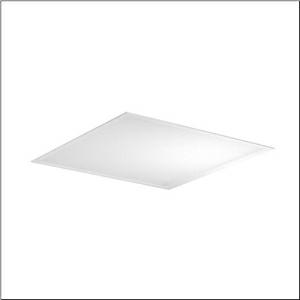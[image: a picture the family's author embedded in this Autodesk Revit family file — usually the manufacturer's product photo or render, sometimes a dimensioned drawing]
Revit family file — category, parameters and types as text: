
# Revit family: apollon_31_square_51mp12wd2m42
name_source: partatom
category: Lighting Fixtures
units: mm (PartAtom-declared; Revit-internal decimal feet)

## family parameters
Cut with Voids When Loaded = No
Host = Face
Light Source = No
Part Type = Normal
Room Calculation Point = No
Round Connector Dimension = Use Diameter
Shared = No

## types (1)
- --- (1 x LED, 4000 lm, 27.5 W, 4000K)
    Apparent Load = 28 VA
    CIE Flux Codes = 62 87 97 100 100
    Color Rendering = 80
    Color Temperature = 4000K
    Default Elevation = 1800 mm
    Description = Apollon 31 square, office luminaire, primary optical cover: micro prismatic cover, of PMMA, CAT 2 (L<= 3000cd/m²), light emission: direct distribution, primary light characteristic: symmetric, installation type: lay-in mounting, recessed, LED, rated luminous flux: 4.000lm, luminous efficacy: 142lm/W, light colour: 830/840, colour temperature: 3000/4000K, control gear: DALI 2, Multilumen, with terminal, 5-pole, mains connection: 220..240V, AC/DC, 0/50..60Hz, rated input power: 28W, suitable for self-contained emergency lighting element 58DB00B013A with integrated self-test function according to EN 60598-2-22, housing, of aluminium, coated, traffic white (RAL 9016), module: M600, length: 595mm, width: 595mm, height: 62mm, housing upper side, of sheet steel, coated, protection rating (complete): IP20, protection rating (lamp compartment, on room side): IP40, insulation class (complete): insulation class II (safety insulation), certification: CE, ENEC, impact resistance: IK03, permissible operating ambient temperature: -20..+40°C, standard: EN 60598-2-22, corresponds to IFS (International Featured Standards) requirements for safety and quality in the food industry, packaging unit: 1 piece
    Height = 0 mm  [stored 0 ft]
    Lamp = 1 x LED
    Lamp Light Flux = 4000 lm
    Lamp Power = 27.5 W
    Lamp count = 1
    Length = 595 mm
    Luminous efficacy = 145 lm/W
    Manufacturer = Siteco
    ModVariant = No
    Model = 51MP12WD2M42
    Mounting Place = Ceiling
    Mounting Type = Recessed
    Number of Poles = 1
    OnlyDefault = Yes
    Power Factor = 1
    Product Name = Apollon 31 square
    Product group = office luminaire | ceiling recessed
    ProductGroupID = 400
    Protection Class = Protection class II
    Protection Degree = IP 20
    RLX_Detail_Level = 1
    RLX_Emergency_Light_Flux = 0 lm
    RLX_Emergency_Type = 0
    RLX_Emergency_Type_DB = No
    RlxData = <blob elided: 13109 chars, md5=fbf19d5b>
    Socket = socket
    Standby Power = 0 W
    System Light Flux = 4000 lm
    System Power = 28 W
    Type Comments = factory setting: colour temperature 4000K
    Type Image = l_1291035.jpg
    URL = http://relux.com
    VarID = @adj_084357
    Voltage = 0 V
    Weight = 0.00 kg
    Width = 595 mm

note: [stored X ft] marks values corroborated as IEEE doubles in the binary element streams (Revit-internal decimal feet)

## geometry (parser evidence)
native form markers: Sweep x10
no freeform markers — native parametric forms only
